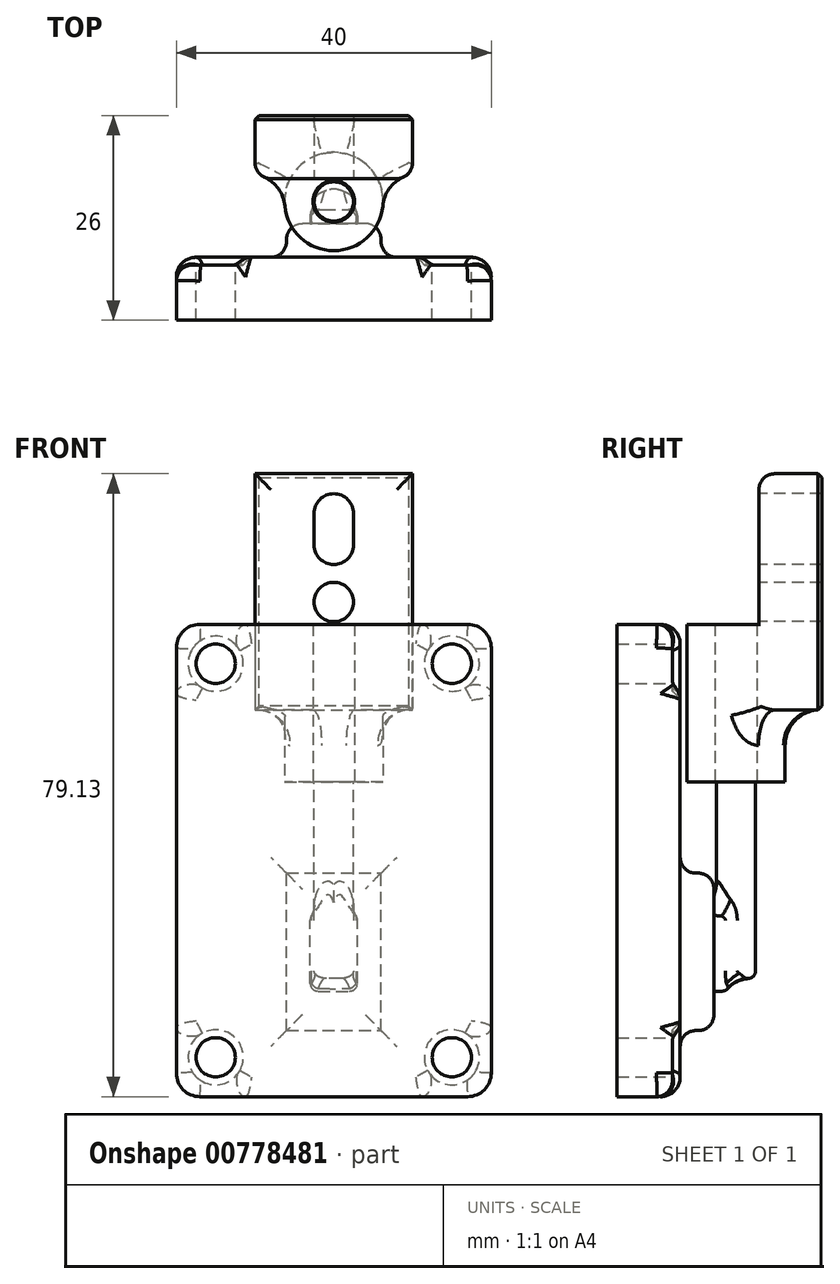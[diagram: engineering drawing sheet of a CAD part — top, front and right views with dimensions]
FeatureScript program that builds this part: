
annotation { "Feature Type Name" : "Feature", "Feature Type Description" : "" }
export const myFeature = defineFeature(function(context is Context, id is Id, definition is map)
    precondition{}
    {
        {
            var Q0;
            Q0=qCreatedBy(makeId("Front.planeOp"),FACE);
            var sketch = newSketch(context, id + "F0", { "sketchPlane" : qUnion([Q0])});
            skLineSegment(sketch, "E0.bottom", {"start": v(17, -30) * mm, "end": v(-17, -30) * mm});
            skLineSegment(sketch, "E0.top", {"start": v(17, 30) * mm, "end": v(-17, 30) * mm});
            skLineSegment(sketch, "E0.left", {"start": v(20, -27) * mm, "end": v(20, 27) * mm});
            skLineSegment(sketch, "E0.right", {"start": v(-20, -27) * mm, "end": v(-20, 27) * mm});
            skPoint(sketch, "E0.middle", {"position": v(0, 0) * mm});
            skPoint(sketch, "E1.visualSharp", {"position": v(-20, 30) * mm});
            skArc(sketch, "E1.filletArc", {"start": v(-17, 30) * mm, "mid": v(-19.12, 29.12) * mm, "end": v(-20, 27) * mm});
            skPoint(sketch, "E2", {"position": v(-15, 25) * mm});
            skPoint(sketch, "E3.MirrorP", {"position": v(15, 25) * mm});
            skArc(sketch, "E4.MirrorCS", {"start": v(17, 30) * mm, "mid": v(19.12, 29.12) * mm, "end": v(20, 27) * mm});
            skPoint(sketch, "E5.MirrorP", {"position": v(20, 30) * mm});
            skPoint(sketch, "E6.MirrorP", {"position": v(-15, -25) * mm});
            skPoint(sketch, "E7.MirrorP", {"position": v(15, -25) * mm});
            skPoint(sketch, "E8.MirrorP", {"position": v(20, -30) * mm});
            skArc(sketch, "E9.MirrorCS", {"start": v(17, -30) * mm, "mid": v(19.12, -29.12) * mm, "end": v(20, -27) * mm});
            skArc(sketch, "E10.MirrorCS", {"start": v(-17, -30) * mm, "mid": v(-19.12, -29.12) * mm, "end": v(-20, -27) * mm});
            skPoint(sketch, "E11.orphan", {"position": v(-20, -30) * mm});
            skSolve(sketch);
        }
        {
            var Q0;
            Q0 = qSketchRegion(id + "F0", true);
            extrude(context, id + "F1", {"entities" : qUnion([Q0]), "depth" : 8 * mm, "offsetDistance" : 25 * mm});
        }
        {
            var Q0;
            Q0=sQuery(id+"F0.wireOp",VERTEX,"E7.MirrorP");
            var Q1;
            Q1=sQuery(id+"F0.wireOp",VERTEX,"E6.MirrorP");
            var Q2;
            Q2=sQuery(id+"F0.wireOp",VERTEX,"E2");
            var Q3;
            Q3=sQuery(id+"F0.wireOp",VERTEX,"E3.MirrorP");
            var Q4;
            Q4=makeQuery(id+"F1.opExtrude","SWEPT_BODY",BODY,{"disambiguationData":[OSD([sQuery(id+"F0.wireOp",EDGE,"E0.bottom"),sQuery(id+"F0.wireOp",EDGE,"E0.top"),sQuery(id+"F0.wireOp",EDGE,"E0.left"),sQuery(id+"F0.wireOp",EDGE,"E0.right"),sQuery(id+"F0.wireOp",EDGE,"E1.filletArc"),sQuery(id+"F0.wireOp",EDGE,"E4.MirrorCS"),sQuery(id+"F0.wireOp",EDGE,"E9.MirrorCS"),sQuery(id+"F0.wireOp",EDGE,"E10.MirrorCS")])]});
            hole(context, id + "F2", {"style" : HoleStyle.C_BORE, "endStyle" : HoleEndStyle.BLIND, "oppositeDirection" : true, "holeDiameter" : 5 * mm, "cBoreDiameter" : 7 * mm, "cBoreDepth" : 1 * mm, "majorDiameter" : 8 * mm, "holeDepth" : 15.75 * mm, "isTappedThrough" : true, "tappedDepth" : 12 * mm, "tapClearance" : 3, "startFromSketch" : true, "locations" : qUnion([Q0, Q1, Q2, Q3]), "scope" : qUnion([Q4])});
        }
        {
            var Q0;
            Q0=makeQuery(id+"F1.opExtrude","CAP_EDGE",EDGE,{"disambiguationData":[OSD([sQuery(id+"F0.wireOp",EDGE,"E0.top")])],"isStart":true});
            fillet(context, id + "F3", {"entities" : qUnion([Q0]), "radius" : 2.5 * mm, "tangentPropagation" : true, "allowEdgeOverflow" : false});
        }
        {
            var Q0;
            Q0=qCreatedBy(makeId("Right.planeOp"),FACE);
            var sketch = newSketch(context, id + "F4", { "sketchPlane" : qUnion([Q0])});
            skLineSegment(sketch, "E12.bottom", {"start": v(4.3, -21.6) * mm, "end": v(-3.7, -21.6) * mm});
            skLineSegment(sketch, "E12.top", {"start": v(4.3, -1.6) * mm, "end": v(-3.7, -1.6) * mm});
            skLineSegment(sketch, "E12.left", {"start": v(4.3, -21.6) * mm, "end": v(4.3, -1.6) * mm});
            skLineSegment(sketch, "E12.right", {"start": v(-3.7, -21.6) * mm, "end": v(-3.7, -1.6) * mm});
            skPoint(sketch, "E12.middle", {"position": v(0.3, -11.6) * mm});
            skSolve(sketch);
        }
        {
            var Q0;
            Q0 = qSketchRegion(id + "F4", true);
            extrude(context, id + "F5", {"entities" : qUnion([Q0]), "operationType" : NewBodyOperationType.ADD, "endBound" : BoundingType.SYMMETRIC, "depth" : 12 * mm, "offsetDistance" : 25 * mm});
        }
        {
            var Q0;
            Q0=makeQuery(id+"F5.opExtrude","SWEPT_EDGE",EDGE,{"disambiguationData":[OSD([sQuery(id+"F4.wireOp",EDGE,"E12.top"),sQuery(id+"F4.wireOp",EDGE,"E12.left")])]});
            var Q1;
            Q1=makeQuery(id+"F5.opExtrude","CAP_EDGE",EDGE,{"disambiguationData":[OSD([sQuery(id+"F4.wireOp",EDGE,"E12.left")])],"isStart":false});
            var Q2;
            Q2=makeQuery(id+"F5.opExtrude","CAP_EDGE",EDGE,{"disambiguationData":[OSD([sQuery(id+"F4.wireOp",EDGE,"E12.left")])],"isStart":true});
            var Q3;
            Q3=makeQuery(id+"F5.opExtrude","SWEPT_EDGE",EDGE,{"disambiguationData":[OSD([sQuery(id+"F4.wireOp",EDGE,"E12.bottom"),sQuery(id+"F4.wireOp",EDGE,"E12.left")])]});
            var Q4;
            Q4=makeQuery(id+"F1.opExtrude","CAP_FACE",FACE,{"disambiguationData":[OSD([sQuery(id+"F0.wireOp",EDGE,"E0.bottom"),sQuery(id+"F0.wireOp",EDGE,"E0.top"),sQuery(id+"F0.wireOp",EDGE,"E0.left"),sQuery(id+"F0.wireOp",EDGE,"E0.right"),sQuery(id+"F0.wireOp",EDGE,"E1.filletArc"),sQuery(id+"F0.wireOp",EDGE,"E4.MirrorCS"),sQuery(id+"F0.wireOp",EDGE,"E9.MirrorCS"),sQuery(id+"F0.wireOp",EDGE,"E10.MirrorCS")])],"isStart":true});
            fillet(context, id + "F6", {"entities" : qUnion([Q0, Q1, Q2, Q3, Q4]), "radius" : 2 * mm, "tangentPropagation" : true, "allowEdgeOverflow" : false});
        }
        {
            var Q0;
            Q0=makeQuery(id+"F5.opExtrude","SWEPT_FACE",FACE,{"disambiguationData":[OSD([sQuery(id+"F4.wireOp",EDGE,"E12.left")])]});
            var sketch = newSketch(context, id + "F7", { "sketchPlane" : qUnion([Q0])});
            skLineSegment(sketch, "E13.bottom", {"start": v(2, -16.6) * mm, "end": v(-2, -16.6) * mm});
            skLineSegment(sketch, "E13.top", {"start": v(2, -6.6) * mm, "end": v(-2, -6.6) * mm});
            skLineSegment(sketch, "E13.left", {"start": v(3, -15.6) * mm, "end": v(3, -7.6) * mm});
            skLineSegment(sketch, "E13.right", {"start": v(-3, -15.6) * mm, "end": v(-3, -7.6) * mm});
            skPoint(sketch, "E13.middle", {"position": v(0, -11.6) * mm});
            skPoint(sketch, "E13.middle.positionSnap0", {"position": v(-4, -11.6) * mm});
            skPoint(sketch, "E13.middle.positionSnap1", {"position": v(0, -3.6) * mm});
            skPoint(sketch, "E13.centerSnap0", {"position": v(-4, -11.6) * mm});
            skPoint(sketch, "E13.centerSnap1", {"position": v(0, -3.6) * mm});
            skPoint(sketch, "E14.visualSharp", {"position": v(-3, -6.6) * mm});
            skArc(sketch, "E14.filletArc", {"start": v(-2, -6.6) * mm, "mid": v(-2.7, -6.9) * mm, "end": v(-3, -7.6) * mm});
            skPoint(sketch, "E15.visualSharp", {"position": v(3, -6.6) * mm});
            skArc(sketch, "E15.filletArc", {"start": v(3, -7.6) * mm, "mid": v(2.7, -6.9) * mm, "end": v(2, -6.6) * mm});
            skPoint(sketch, "E16.visualSharp", {"position": v(3, -16.6) * mm});
            skArc(sketch, "E16.filletArc", {"start": v(2, -16.6) * mm, "mid": v(2.7, -16.3) * mm, "end": v(3, -15.6) * mm});
            skPoint(sketch, "E17.visualSharp", {"position": v(-3, -16.6) * mm});
            skArc(sketch, "E17.filletArc", {"start": v(-3, -15.6) * mm, "mid": v(-2.7, -16.3) * mm, "end": v(-2, -16.6) * mm});
            skSolve(sketch);
        }
        {
            var Q0;
            Q0=qCreatedBy(makeId("Top.planeOp"),FACE);
            cPlane(context, id + "F8", {"entities" : qUnion([Q0]), "cplaneType" : CPlaneType.OFFSET, "offset" : 10 * mm, "width" : 150 * mm, "height" : 150 * mm});
        }
        {
            var Q0;
            Q0=qCreatedBy(id+"F8.planeOp",FACE);
            var sketch = newSketch(context, id + "F9", { "sketchPlane" : qUnion([Q0])});
            skArc(sketch, "E18", {"start": v(1.73, 8.9) * mm, "mid": v(-0.05, 9.59) * mm, "end": v(-1.8, 8.82) * mm});
            skArc(sketch, "E19", {"start": v(-1.8, 8.82) * mm, "mid": v(-2.5, 7.24) * mm, "end": v(-2, 5.6) * mm});
            skArc(sketch, "E20", {"start": v(-2, 5.6) * mm, "mid": v(-0.22, 4.6) * mm, "end": v(1.7, 5.26) * mm});
            skArc(sketch, "E21", {"start": v(1.7, 5.26) * mm, "mid": v(2.5, 7.07) * mm, "end": v(1.73, 8.9) * mm});
            skSolve(sketch);
        }
        {
            var Q0;
            Q0=makeQuery(id+"F9.imprint","IMPRINT",FACE,{"disambiguationData":[TD([[makeQuery(id+"F9.imprint","IMPRINT",EDGE,{"derivedFrom":sQuery(id+"F9.wireOp",EDGE,"E18")}),1.0]])]});
            extrude(context, id + "F10", {"entities" : qUnion([Q0]), "operationType" : NewBodyOperationType.ADD, "oppositeDirection" : true, "depth" : 25 * mm, "offsetDistance" : 25 * mm});
        }
        {
            var Q0;
            Q0=makeQuery(id+"F7.imprint","IMPRINT",FACE,{"disambiguationData":[TD([[makeQuery(id+"F7.imprint","IMPRINT",EDGE,{"derivedFrom":sQuery(id+"F7.wireOp",EDGE,"E13.bottom")}),-1.0]])]});
            extrude(context, id + "F11", {"entities" : qUnion([Q0]), "operationType" : NewBodyOperationType.ADD, "depth" : 2 * mm, "offsetDistance" : 25 * mm});
        }
        {
            var Q0;
            Q0=makeQuery(id+"F11.opExtrude","CAP_EDGE",EDGE,{"disambiguationData":[OSD([sQuery(id+"F7.wireOp",EDGE,"E13.bottom")])],"isStart":false});
            fillet(context, id + "F12", {"entities" : qUnion([Q0]), "radius" : 1 * mm, "tangentPropagation" : true, "allowEdgeOverflow" : false});
        }
        {
            var Q0;
            Q0=qCreatedBy(id+"F8.planeOp",FACE);
            var sketch = newSketch(context, id + "F13", { "sketchPlane" : qUnion([Q0])});
            skCircle(sketch, "E22", {"center": v(0, 7.09) * mm, "radius": 2.64 * mm});
            skCircle(sketch, "E23", {"center": v(0, 7.09) * mm, "radius": 6.25 * mm});
            skSolve(sketch);
        }
        {
            var Q0;
            Q0=makeQuery(id+"F13.imprint","IMPRINT",FACE,{"disambiguationData":[TD([[makeQuery(id+"F13.imprint","IMPRINT",EDGE,{"derivedFrom":sQuery(id+"F13.wireOp",EDGE,"E22")}),-1.0]])]});
            extrude(context, id + "F14", {"entities" : qUnion([Q0]), "depth" : 20 * mm, "offsetDistance" : 25 * mm});
        }
        {
            var Q0;
            Q0=qCreatedBy(makeId("Front.planeOp"),FACE);
            cPlane(context, id + "F15", {"entities" : qUnion([Q0]), "cplaneType" : CPlaneType.OFFSET, "offset" : 10 * mm, "oppositeDirection" : true, "width" : 150 * mm, "height" : 150 * mm});
        }
        {
            var Q0;
            Q0=qCreatedBy(id+"F15.planeOp",FACE);
            var sketch = newSketch(context, id + "F16", { "sketchPlane" : qUnion([Q0])});
            skLineSegment(sketch, "E24.bottom", {"start": v(10, 49.13) * mm, "end": v(-10, 49.13) * mm});
            skLineSegment(sketch, "E24.top", {"start": v(10, 19.13) * mm, "end": v(-10, 19.13) * mm});
            skLineSegment(sketch, "E24.left", {"start": v(10, 49.13) * mm, "end": v(10, 19.13) * mm});
            skLineSegment(sketch, "E24.right", {"start": v(-10, 49.13) * mm, "end": v(-10, 19.13) * mm});
            skPoint(sketch, "E24.middle", {"position": v(0, 34.13) * mm});
            skSolve(sketch);
        }
        {
            var Q0;
            Q0 = qSketchRegion(id + "F16", true);
            extrude(context, id + "F17", {"entities" : qUnion([Q0]), "operationType" : NewBodyOperationType.ADD, "oppositeDirection" : true, "depth" : 8 * mm, "offsetDistance" : 25 * mm});
        }
        {
            var Q0;
            Q0=makeQuery(id+"F17.opExtrude","CAP_FACE",FACE,{"disambiguationData":[OSD([sQuery(id+"F16.wireOp",EDGE,"E24.bottom"),sQuery(id+"F16.wireOp",EDGE,"E24.top"),sQuery(id+"F16.wireOp",EDGE,"E24.left"),sQuery(id+"F16.wireOp",EDGE,"E24.right")])],"isStart":false});
            chamfer(context, id + "F18", {"entities" : qUnion([Q0]), "width" : .5 * mm, "tangentPropagation" : true});
        }
        {
            var Q0;
            Q0=makeQuery(id+"F17.opExtrude","CAP_EDGE",EDGE,{"disambiguationData":[OSD([sQuery(id+"F16.wireOp",EDGE,"E24.left")])],"isStart":true});
            var Q1;
            Q1=makeQuery(id+"F17.opExtrude","CAP_EDGE",EDGE,{"disambiguationData":[OSD([sQuery(id+"F16.wireOp",EDGE,"E24.bottom")])],"isStart":true});
            var Q2;
            Q2=makeQuery(id+"F17.opExtrude","CAP_EDGE",EDGE,{"disambiguationData":[OSD([sQuery(id+"F16.wireOp",EDGE,"E24.right")])],"isStart":true});
            var Q3;
            {var subQ0=sQuery(id+"F16.wireOp",EDGE,"E24.right");var subQ1=sQuery(id+"F16.wireOp",EDGE,"E24.top");Q3=makeQuery(id+"F17.boolean.opBoolean","SPLIT",EDGE,{"disambiguationData":[TD([makeQuery(id+"F17.opExtrude","SWEPT_FACE",FACE,{"disambiguationData":[OSD([subQ0])]})])],"derivedFrom":makeQuery(id+"F17.opExtrude","CAP_EDGE",EDGE,{"disambiguationData":[OSD([subQ1])],"isStart":true})});}
            var Q4;
            {var subQ0=sQuery(id+"F16.wireOp",EDGE,"E24.left");var subQ1=sQuery(id+"F16.wireOp",EDGE,"E24.top");Q4=makeQuery(id+"F17.boolean.opBoolean","SPLIT",EDGE,{"disambiguationData":[TD([makeQuery(id+"F17.opExtrude","SWEPT_FACE",FACE,{"disambiguationData":[OSD([subQ0])]})])],"derivedFrom":makeQuery(id+"F17.opExtrude","CAP_EDGE",EDGE,{"disambiguationData":[OSD([subQ1])],"isStart":true})});}
            fillet(context, id + "F19", {"entities" : qUnion([Q0, Q1, Q2, Q3, Q4]), "radius" : 2 * mm, "tangentPropagation" : true, "allowEdgeOverflow" : false});
        }
        {
            var Q0;
            Q0=makeQuery(id+"F17.opExtrude","CAP_FACE",FACE,{"disambiguationData":[OSD([sQuery(id+"F16.wireOp",EDGE,"E24.bottom"),sQuery(id+"F16.wireOp",EDGE,"E24.top"),sQuery(id+"F16.wireOp",EDGE,"E24.left"),sQuery(id+"F16.wireOp",EDGE,"E24.right")])],"isStart":true});
            var sketch = newSketch(context, id + "F20", { "sketchPlane" : qUnion([Q0])});
            skCircle(sketch, "E25", {"center": v(0, 32.84) * mm, "radius": 2.5 * mm});
            skArc(sketch, "E26", {"start": v(-2.5, 40.09) * mm, "mid": v(0, 37.59) * mm, "end": v(2.5, 40.09) * mm});
            skLineSegment(sketch, "E27", {"start": v(-2.5, 44.1) * mm, "end": v(-2.5, 40.09) * mm});
            skLineSegment(sketch, "E28", {"start": v(2.5, 44.1) * mm, "end": v(2.5, 40.09) * mm});
            skArc(sketch, "E29.trimOffspring", {"start": v(2.5, 44.1) * mm, "mid": v(0, 46.6) * mm, "end": v(-2.5, 44.1) * mm});
            skSolve(sketch);
        }
        {
            var Q0;
            Q0 = qSketchRegion(id + "F20", true);
            extrude(context, id + "F21", {"entities" : qUnion([Q0]), "operationType" : NewBodyOperationType.REMOVE, "oppositeDirection" : true, "depth" : 25 * mm, "offsetDistance" : 25 * mm});
        }
        {
            var Q0;
            {var subQ0=makeQuery(id+"F14.opExtrude","SWEPT_FACE",FACE,{"disambiguationData":[OSD([sQuery(id+"F13.wireOp",EDGE,"E23")])]});var subQ1=sQuery(id+"F16.wireOp",EDGE,"E24.right");var subQ2=sQuery(id+"F16.wireOp",EDGE,"E24.top");Q0=makeQuery(id+"F19.opFillet","BLEND_EDGE",EDGE,{"blendedFrom":[makeQuery(id+"F17.boolean.opBoolean","SPLIT",EDGE,{"disambiguationData":[TD([makeQuery(id+"F17.opExtrude","SWEPT_FACE",FACE,{"disambiguationData":[OSD([subQ1])]})])],"derivedFrom":makeQuery(id+"F17.opExtrude","CAP_EDGE",EDGE,{"disambiguationData":[OSD([subQ2])],"isStart":true})}),subQ0],"blendedInto":[subQ0]});}
            var Q1;
            Q1=makeQuery(id+"F17.boolean.opBoolean","INTERSECT",EDGE,{"derivedFrom":[makeQuery(id+"F14.opExtrude","SWEPT_FACE",FACE,{"disambiguationData":[OSD([sQuery(id+"F13.wireOp",EDGE,"E23")])]}),makeQuery(id+"F17.opExtrude","SWEPT_FACE",FACE,{"disambiguationData":[OSD([sQuery(id+"F16.wireOp",EDGE,"E24.top")])]})]});
            var Q2;
            {var subQ0=makeQuery(id+"F14.opExtrude","SWEPT_FACE",FACE,{"disambiguationData":[OSD([sQuery(id+"F13.wireOp",EDGE,"E23")])]});var subQ1=sQuery(id+"F16.wireOp",EDGE,"E24.left");var subQ2=sQuery(id+"F16.wireOp",EDGE,"E24.top");Q2=makeQuery(id+"F19.opFillet","BLEND_EDGE",EDGE,{"blendedFrom":[makeQuery(id+"F17.boolean.opBoolean","SPLIT",EDGE,{"disambiguationData":[TD([makeQuery(id+"F17.opExtrude","SWEPT_FACE",FACE,{"disambiguationData":[OSD([subQ1])]})])],"derivedFrom":makeQuery(id+"F17.opExtrude","CAP_EDGE",EDGE,{"disambiguationData":[OSD([subQ2])],"isStart":true})}),subQ0],"blendedInto":[subQ0]});}
            fillet(context, id + "F22", {"entities" : qUnion([Q0, Q1, Q2]), "radius" : 4.5 * mm, "tangentPropagation" : true, "allowEdgeOverflow" : false});
        }
        {
            var Q0;
            Q0=makeQuery(id+"F10.opExtrude","CAP_EDGE",EDGE,{"disambiguationData":[OSD([sQuery(id+"F9.wireOp",EDGE,"E18"),sQuery(id+"F9.wireOp",EDGE,"E19"),sQuery(id+"F9.wireOp",EDGE,"E20"),sQuery(id+"F9.wireOp",EDGE,"E21")])],"isStart":false});
            fillet(context, id + "F23", {"entities" : qUnion([Q0]), "radius" : 1 * mm, "tangentPropagation" : true, "allowEdgeOverflow" : false});
        }
        {
            var Q0;
            Q0=makeQuery(id+"F12.opFillet","BLEND_EDGE",EDGE,{"disambiguationData":[OD(1.0)],"blendedFrom":[makeQuery(id+"F11.opExtrude","CAP_EDGE",EDGE,{"disambiguationData":[OSD([sQuery(id+"F7.wireOp",EDGE,"E13.left")])],"isStart":false}),makeQuery(id+"F10.opExtrude","SWEPT_FACE",FACE,{"disambiguationData":[OSD([sQuery(id+"F9.wireOp",EDGE,"E18"),sQuery(id+"F9.wireOp",EDGE,"E19"),sQuery(id+"F9.wireOp",EDGE,"E20"),sQuery(id+"F9.wireOp",EDGE,"E21")])]})],"blendedInto":[makeQuery(id+"F10.opExtrude","SWEPT_FACE",FACE,{"disambiguationData":[OSD([sQuery(id+"F9.wireOp",EDGE,"E18"),sQuery(id+"F9.wireOp",EDGE,"E19"),sQuery(id+"F9.wireOp",EDGE,"E20"),sQuery(id+"F9.wireOp",EDGE,"E21")])]})]});
            fillet(context, id + "F24", {"entities" : qUnion([Q0]), "radius" : 4 * mm, "tangentPropagation" : true, "allowEdgeOverflow" : false});
        }
    });
